# Revit family: LPD
name_source: partatom
category: Mechanical Equipment
revit_build: Autodesk Revit 2015 (Build: 20140606_1530(x64)
units: mm (PartAtom-declared; Revit-internal decimal feet)

## types (9) — shared parameters
Description = Low Profile Plenum Diffuser
Manufacturer = United Enertech Corporation
Model = LPD
Type Comments = Consult Factory for Max. Sizes
URL = https://unitedenertech.com

## per-type parameters (varying)
| type | B | F | Grille Height | Grille Length | T |
| LPD-1806-5 (2000 cfm) | 1' - 10" | 0' - 8" | 0' - 6" | 1' - 6" | 1' - 2" |
| LPD-2206-6 (2400 cfm) | 2' - 2" | 0' - 8" | 0' - 6" | 1' - 10" | 1' - 4" |
| LPD-2606-7.5 (3000 cfm) | 2' - 6" | 0' - 8" | 0' - 6" | 2' - 2" | 1' - 8" |
| LPD-2608-8.5 (3400 cfm) | 2' - 6" | 0' - 10" | 0' - 8" | 2' - 2" | 1' - 8" |
| LPD-2808-10 (4000 cfm) | 2' - 8" | 0' - 10" | 0' - 8" | 2' - 4" | 1' - 10" |
| LPD-3008-12.5 (5000 cfm) | 2' - 10" | 0' - 10" | 0' - 8" | 2' - 6" | 2' - 0" |
| LPD-3408-15 (6000 cfm) | 3' - 2" | 0' - 10" | 0' - 8" | 2' - 10" | 2' - 4" |
| LPD-4410-20 (8000 cfm) | 4' - 0" | 1' - 0" | 0' - 10" | 3' - 8" | 2' - 6" |
| LPD-4810-25 (10000 cfm) | 4' - 4" | 1' - 0" | 0' - 10" | 4' - 0" | 3' - 0" |

## geometry (parser evidence)
native form markers: Sweep x7
no freeform markers — native parametric forms only
